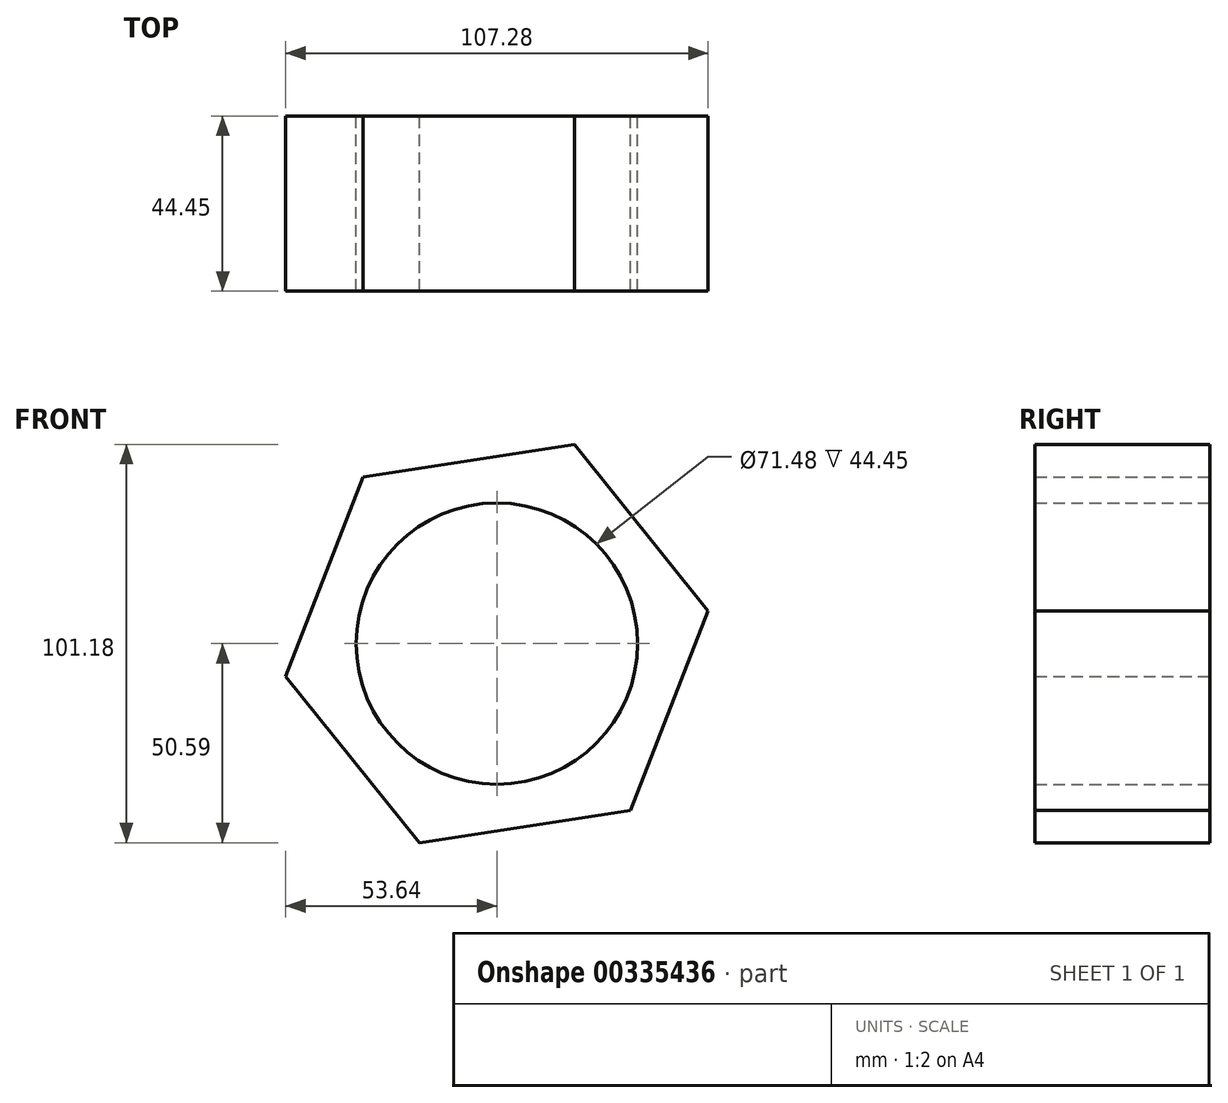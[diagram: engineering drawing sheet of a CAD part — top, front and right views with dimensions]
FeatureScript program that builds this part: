
annotation { "Feature Type Name" : "Feature", "Feature Type Description" : "" }
export const myFeature = defineFeature(function(context is Context, id is Id, definition is map)
    precondition{}
    {
        {
            var Q0;
            Q0=qCreatedBy(makeId("Front.planeOp"),FACE);
            var sketch = newSketch(context, id + "F0", { "sketchPlane" : qUnion([Q0])});
            skCircle(sketch, "E0.cCircle", {"center": v(0, 0) * mm, "radius": 47 * mm, "construction": true});
            skLineSegment(sketch, "E0.0", {"start": v(53.64, 8.27) * mm, "end": v(33.98, -42.32) * mm});
            skLineSegment(sketch, "E0.1", {"start": v(33.98, -42.32) * mm, "end": v(-19.66, -50.59) * mm});
            skLineSegment(sketch, "E0.2", {"start": v(-19.66, -50.59) * mm, "end": v(-53.64, -8.27) * mm});
            skLineSegment(sketch, "E0.3", {"start": v(-53.64, -8.27) * mm, "end": v(-33.98, 42.32) * mm});
            skLineSegment(sketch, "E0.4", {"start": v(-33.98, 42.32) * mm, "end": v(19.66, 50.59) * mm});
            skLineSegment(sketch, "E0.5", {"start": v(19.66, 50.59) * mm, "end": v(53.64, 8.27) * mm});
            skPoint(sketch, "E0.0.midPoint", {"position": v(43.81, -17.03) * mm});
            skCircle(sketch, "E1", {"center": v(0, 0) * mm, "radius": 35.74 * mm});
            skSolve(sketch);
        }
        {
            var Q0;
            Q0=makeQuery(id+"F0.imprint","IMPRINT",FACE,{"disambiguationData":[TD([[makeQuery(id+"F0.imprint","IMPRINT",EDGE,{"derivedFrom":sQuery(id+"F0.wireOp",EDGE,"E0.0")}),-1.0]])]});
            extrude(context, id + "F1", {"entities" : qUnion([Q0]), "depth" : 44.45 * mm});
        }
    });
